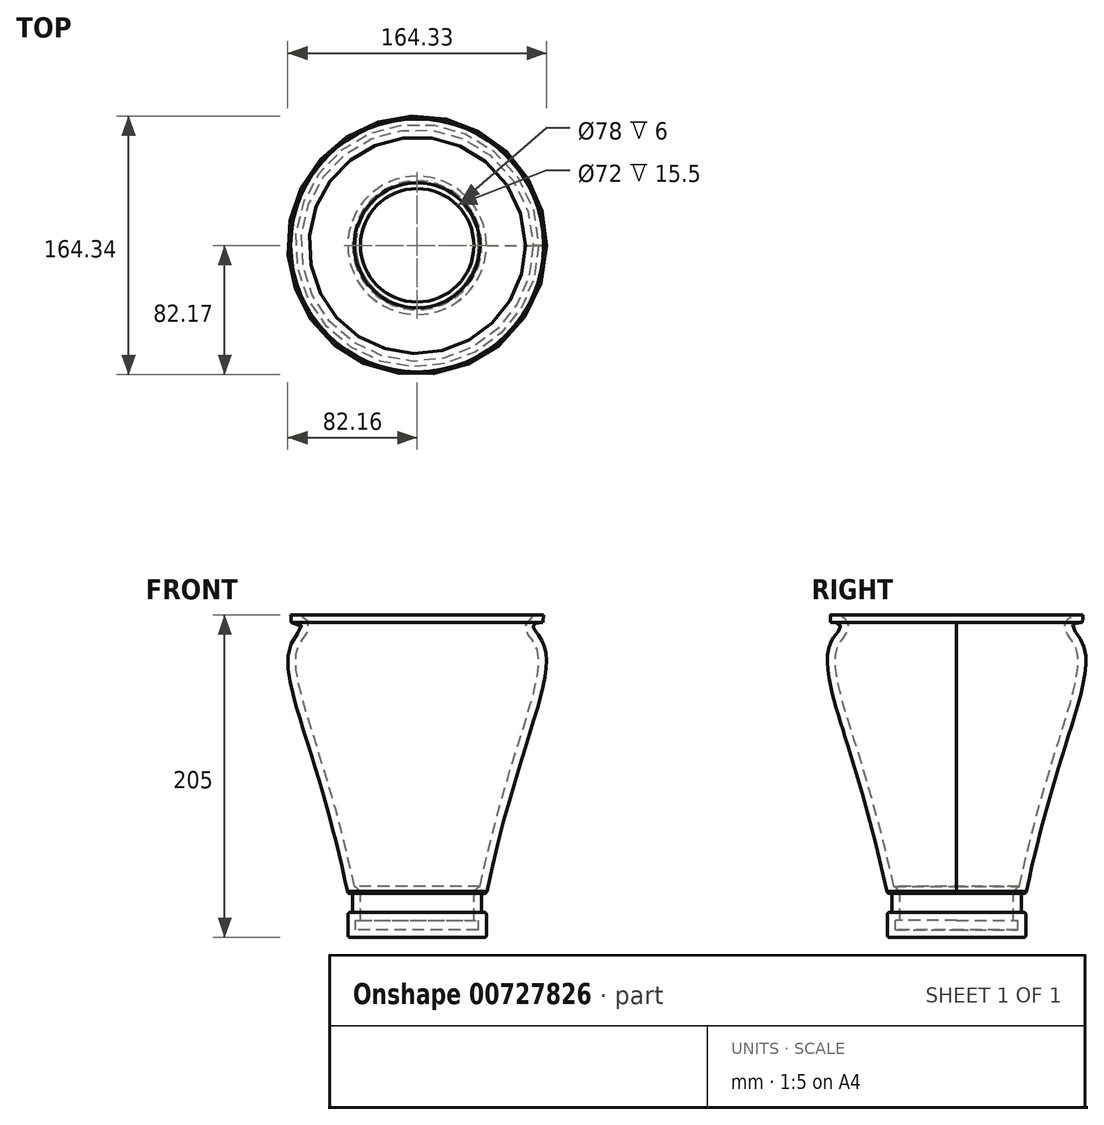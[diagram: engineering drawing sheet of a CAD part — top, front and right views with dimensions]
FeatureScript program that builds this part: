
annotation { "Feature Type Name" : "Feature", "Feature Type Description" : "" }
export const myFeature = defineFeature(function(context is Context, id is Id, definition is map)
    precondition{}
    {
        {
            var Q0;
            Q0=qCreatedBy(makeId("Front.planeOp"),FACE);
            var sketch = newSketch(context, id + "F0", { "sketchPlane" : qUnion([Q0])});
            skLineSegment(sketch, "E0", {"start": v(0, 0) * mm, "end": v(0, -200) * mm});
            skLineSegment(sketch, "E1", {"start": v(0, -200) * mm, "end": v(44, -200) * mm});
            skLineSegment(sketch, "E2", {"start": v(0, 0) * mm, "end": v(80, 0) * mm});
            skLineSegment(sketch, "E3", {"start": v(44, -200) * mm, "end": v(44, -184) * mm});
            skLineSegment(sketch, "E4", {"start": v(44, -184) * mm, "end": v(41, -184) * mm});
            skLineSegment(sketch, "E5", {"start": v(41, -184) * mm, "end": v(41, -172) * mm});
            skLineSegment(sketch, "E6", {"start": v(41, -172) * mm, "end": v(44, -172) * mm});
            skFitSpline(sketch, "E7", {"points": [v(44, -172) * mm, v(78.33, -9.9) * mm, v(80, 0) * mm], "startDerivative": vector(81.3, 383.76) * mm, "endDerivative": vector(165.88, 0) * mm});
            skSolve(sketch);
        }
        {
            var Q0;
            Q0 = qSketchRegion(id + "F0", true);
            var Q1;
            Q1=sQuery(id+"F0.wireOp",EDGE,"E0");
            revolve(context, id + "F1", {"surfaceOperationType" : NewSurfaceOperationType.NEW, "entities" : qUnion([Q0]), "axis" : qUnion([Q1]), "revolveType" : RevolveType.FULL});
        }
        {
            var Q0;
            Q0=makeQuery(id+"F1.opRevolve","SWEPT_FACE",FACE,{"disambiguationData":[OSD([sQuery(id+"F0.wireOp",EDGE,"E1")])]});
            var Q1;
            Q1=makeQuery(id+"F1.opRevolve","SWEPT_EDGE",EDGE,{"disambiguationData":[OSD([sQuery(id+"F0.wireOp",EDGE,"E3"),sQuery(id+"F0.wireOp",EDGE,"E4")])]});
            var Q2;
            Q2=makeQuery(id+"F1.opRevolve","SWEPT_EDGE",EDGE,{"disambiguationData":[OSD([sQuery(id+"F0.wireOp",EDGE,"E6"),sQuery(id+"F0.wireOp",EDGE,"E7")])]});
            var Q3;
            Q3=makeQuery(id+"F1.opRevolve","SWEPT_EDGE",EDGE,{"disambiguationData":[OSD([sQuery(id+"F0.wireOp",EDGE,"E5"),sQuery(id+"F0.wireOp",EDGE,"E6")])]});
            fillet(context, id + "F2", {"entities" : qUnion([Q0, Q1, Q2, Q3]), "radius" : 1.5 * mm, "tangentPropagation" : true, "allowEdgeOverflow" : false});
        }
        {
            var Q0;
            Q0=qCreatedBy(makeId("Front.planeOp"),FACE);
            var sketch = newSketch(context, id + "F3", { "sketchPlane" : qUnion([Q0])});
            skLineSegment(sketch, "E8", {"start": v(0, 0) * mm, "end": v(80, 0) * mm});
            skLineSegment(sketch, "E9", {"start": v(0, 0) * mm, "end": v(0, 40) * mm});
            skLineSegment(sketch, "E10", {"start": v(0, 40) * mm, "end": v(120, 40) * mm});
            skArc(sketch, "E11", {"start": v(80, 0) * mm, "mid": v(91.72, 28.28) * mm, "end": v(120, 40) * mm});
            skSolve(sketch);
        }
        {
            var Q0;
            Q0 = qSketchRegion(id + "F3", true);
            var Q1;
            Q1=sQuery(id+"F3.wireOp",EDGE,"E9");
            revolve(context, id + "F4", {"operationType" : NewBodyOperationType.ADD, "surfaceOperationType" : NewSurfaceOperationType.NEW, "entities" : qUnion([Q0]), "axis" : qUnion([Q1]), "revolveType" : RevolveType.FULL});
        }
        {
            var Q0;
            Q0=makeQuery(id+"F4.opRevolve","SWEPT_FACE",FACE,{"disambiguationData":[OSD([sQuery(id+"F3.wireOp",EDGE,"E10")])]});
            var Q1;
            Q1=makeQuery(id+"F4.opRevolve","SWEPT_FACE",FACE,{"disambiguationData":[OSD([sQuery(id+"F3.wireOp",EDGE,"E11")])]});
            shell(context, id + "F5", {"entities" : qUnion([Q0, Q1]), "thickness" : 5 * mm});
        }
    });
